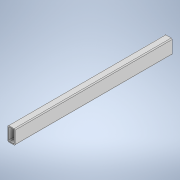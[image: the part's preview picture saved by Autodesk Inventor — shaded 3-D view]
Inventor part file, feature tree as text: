
AUTODESK INVENTOR PART (.ipt)
format: ipt  version: 2020 (Build 240168000, 168)  size: 122,880 bytes
history: native  units: in
note: dims shown in document units (in); Inventor stores cm internally (conversion verified against a paired STEP export)
features: extrude x1, sketch x1
ambient origin geometry x8: Origin, YZ Plane, XZ Plane, XY Plane, X Axis, Y Axis, Z Axis, Center Point
bodies: Solid1 (feature_tree)
feature tree (2):
  extrude  "Extrusion1"  Depth=1.0in
  sketch  "Sketch1"  dims[d0=2.0in d1=1.0in d2=0.125in d3=0.125in d4=0.125in d5=0.125in d6=0.125in d7=0.125in d8=0.125in d9=0.125in d10=0.125in d11=22.0in d12=0.0in]
